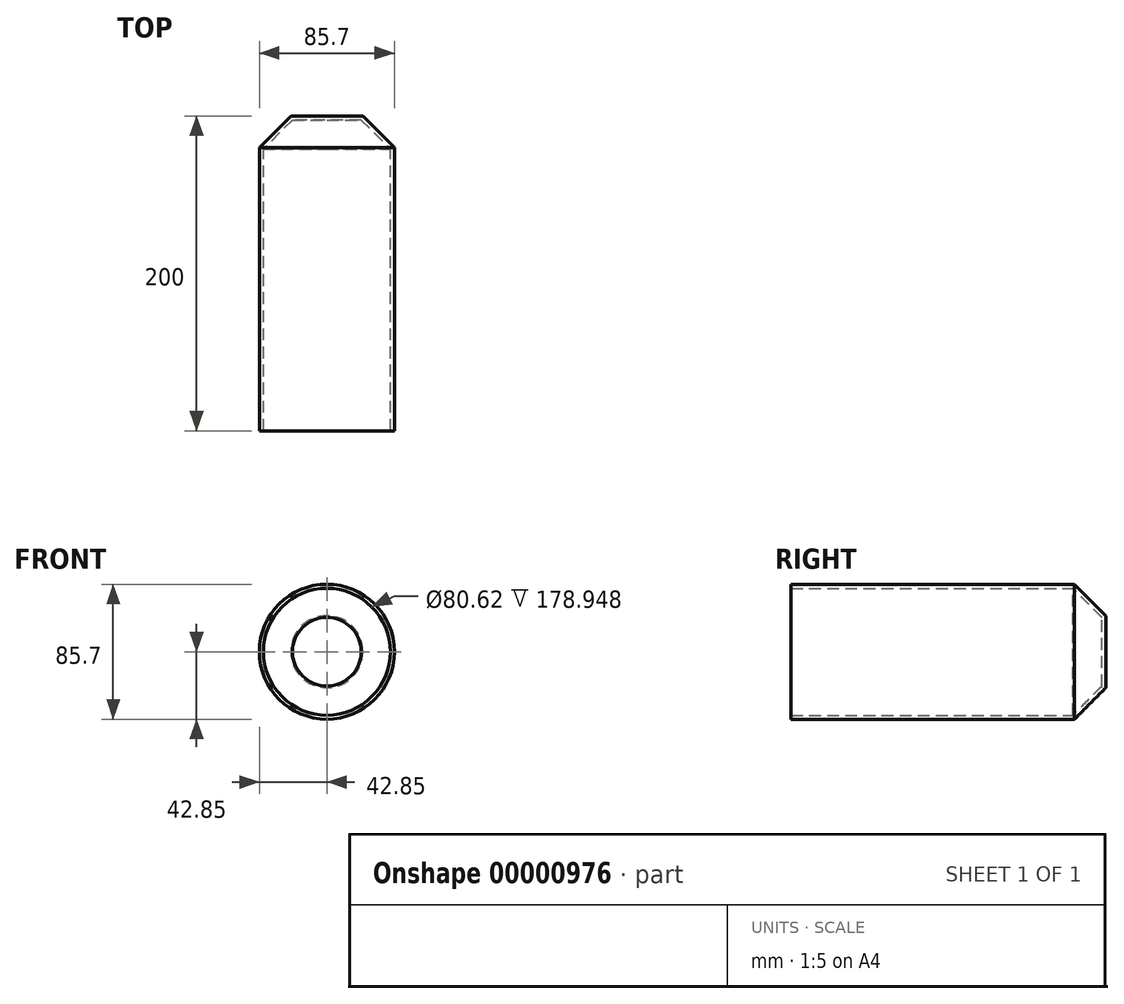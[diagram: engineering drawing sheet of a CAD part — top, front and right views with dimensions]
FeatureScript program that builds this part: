
annotation { "Feature Type Name" : "Feature", "Feature Type Description" : "" }
export const myFeature = defineFeature(function(context is Context, id is Id, definition is map)
    precondition{}
    {
        {
            var Q0;
            Q0=qCreatedBy(makeId("Front.planeOp"),FACE);
            var sketch = newSketch(context, id + "F0", { "sketchPlane" : qUnion([Q0])});
            skCircle(sketch, "E0", {"center": v(0, 0) * mm, "radius": 42.85 * mm});
            skSolve(sketch);
        }
        {
            var Q0;
            Q0=makeQuery(id+"F0.imprint","IMPRINT",FACE,{"disambiguationData":[TD([[makeQuery(id+"F0.imprint","IMPRINT",EDGE,{"derivedFrom":sQuery(id+"F0.wireOp",EDGE,"E0")}),1.0]])]});
            extrude(context, id + "F1", {"entities" : qUnion([Q0]), "depth" : 200 * mm});
        }
        {
            var Q0;
            Q0=makeQuery(id+"F1.opExtrude","CAP_EDGE",EDGE,{"disambiguationData":[OSD([sQuery(id+"F0.wireOp",EDGE,"E0")])],"isStart":true});
            chamfer(context, id + "F2", {"entities" : qUnion([Q0]), "width" : 20 * mm, "tangentPropagation" : true});
        }
        {
            var Q0;
            Q0=makeQuery(id+"F1.opExtrude","CAP_FACE",FACE,{"disambiguationData":[OSD([sQuery(id+"F0.wireOp",EDGE,"E0")])],"isStart":false});
            shell(context, id + "F3", {"entities" : qUnion([Q0]), "thickness" : 2.54 * mm});
        }
    });
